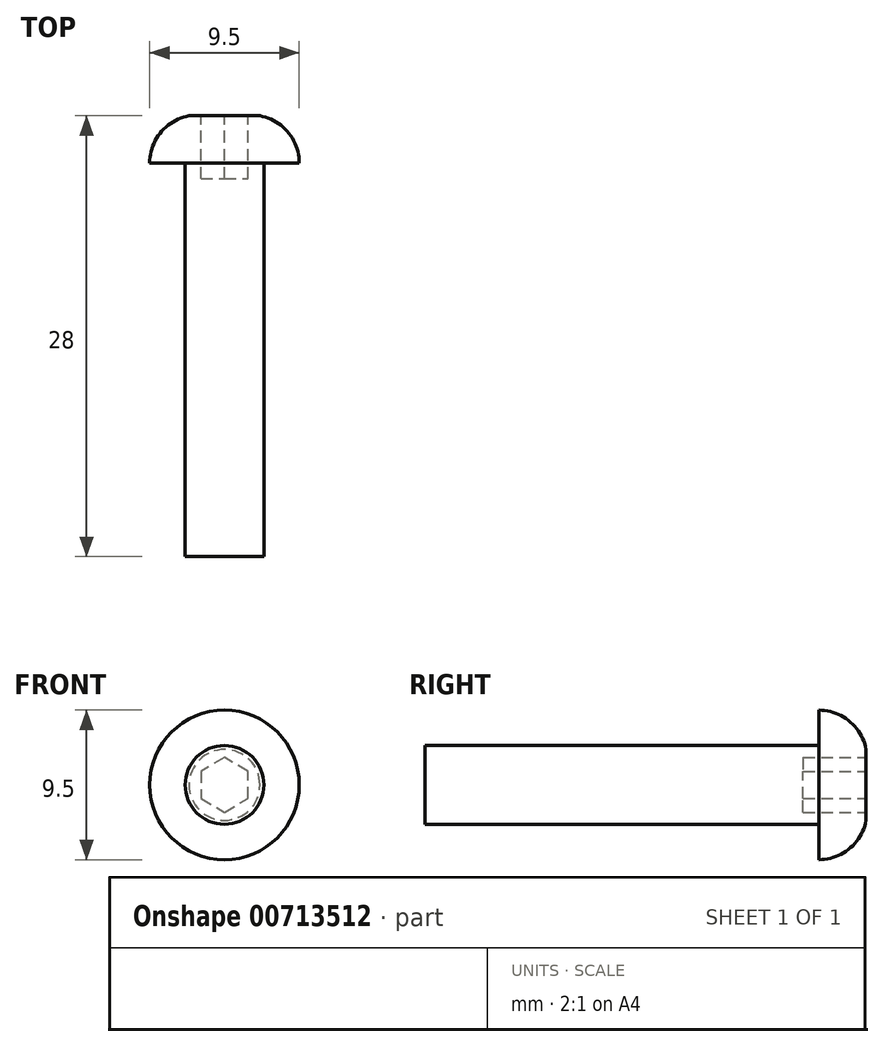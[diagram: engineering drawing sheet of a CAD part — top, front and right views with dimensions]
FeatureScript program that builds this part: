
annotation { "Feature Type Name" : "Feature", "Feature Type Description" : "" }
export const myFeature = defineFeature(function(context is Context, id is Id, definition is map)
    precondition{}
    {
        {
            assignVariable(context, id + "F0", {"name" : "threadedLength", "anyValue" : 25 * mm});
        }
        {
            var Q0;
            Q0=qCreatedBy(makeId("Front.planeOp"),FACE);
            var sketch = newSketch(context, id + "F1", { "sketchPlane" : qUnion([Q0])});
            skCircle(sketch, "E0", {"center": v(0, 0) * mm, "radius": 2.5 * mm});
            skSolve(sketch);
        }
        {
            var Q0;
            Q0=qSketchRegion(id+"F1",true);
            extrude(context, id + "F2", {"entities" : qUnion([Q0]), "depth" : getVariable(context, 'threadedLength'), "offsetDistance" : 25 * mm});
        }
        {
            var Q0;
            Q0=qCreatedBy(makeId("Right.planeOp"),FACE);
            var sketch = newSketch(context, id + "F3", { "sketchPlane" : qUnion([Q0])});
            skLineSegment(sketch, "E1", {"start": v(0, 0) * mm, "end": v(0, 4.75) * mm});
            skLineSegment(sketch, "E2", {"start": v(0, 0) * mm, "end": v(3, 0) * mm});
            skLineSegment(sketch, "E3", {"start": v(3, 0) * mm, "end": v(3, 1.5) * mm});
            skLineSegment(sketch, "E4", {"start": v(3, 1.5) * mm, "end": v(3, 2.25) * mm});
            skArc(sketch, "E5", {"start": v(3, 2.25) * mm, "mid": v(1.95, 4.04) * mm, "end": v(0, 4.75) * mm});
            skSolve(sketch);
        }
        {
            var Q0;
            Q0=qSketchRegion(id+"F3",true);
            var Q1;
            Q1=makeQuery(id+"F2.opExtrude","CAP_EDGE",EDGE,{"disambiguationData":[OSD([sQuery(id+"F1.wireOp",EDGE,"E0")])],"isStart":true});
            revolve(context, id + "F4", {"operationType" : NewBodyOperationType.ADD, "entities" : qUnion([Q0]), "axis" : qUnion([Q1]), "revolveType" : RevolveType.FULL});
        }
        {
            var Q0;
            Q0=makeQuery(id+"F4.opRevolve","SWEPT_FACE",FACE,{"disambiguationData":[OSD([sQuery(id+"F3.wireOp",EDGE,"E3"),sQuery(id+"F3.wireOp",EDGE,"E4")])]});
            var sketch = newSketch(context, id + "F5", { "sketchPlane" : qUnion([Q0])});
            skCircle(sketch, "E6.cCircle", {"center": v(0, 0) * mm, "radius": 1.5 * mm, "construction": true});
            skLineSegment(sketch, "E6.0", {"start": v(-1.5, -0.87) * mm, "end": v(-1.5, 0.87) * mm});
            skLineSegment(sketch, "E6.1", {"start": v(-1.5, 0.87) * mm, "end": v(0, 1.73) * mm});
            skLineSegment(sketch, "E6.2", {"start": v(0, 1.73) * mm, "end": v(1.5, 0.87) * mm});
            skLineSegment(sketch, "E6.3", {"start": v(1.5, 0.87) * mm, "end": v(1.5, -0.87) * mm});
            skLineSegment(sketch, "E6.4", {"start": v(1.5, -0.87) * mm, "end": v(0, -1.73) * mm});
            skLineSegment(sketch, "E6.5", {"start": v(0, -1.73) * mm, "end": v(-1.5, -0.87) * mm});
            skPoint(sketch, "E6.0.midPoint", {"position": v(-1.5, 0) * mm});
            skSolve(sketch);
        }
        {
            var Q0;
            Q0=qSketchRegion(id+"F5",true);
            extrude(context, id + "F6", {"entities" : qUnion([Q0]), "operationType" : NewBodyOperationType.REMOVE, "oppositeDirection" : true, "depth" : 4 * mm, "offsetDistance" : 25 * mm});
        }
    });
